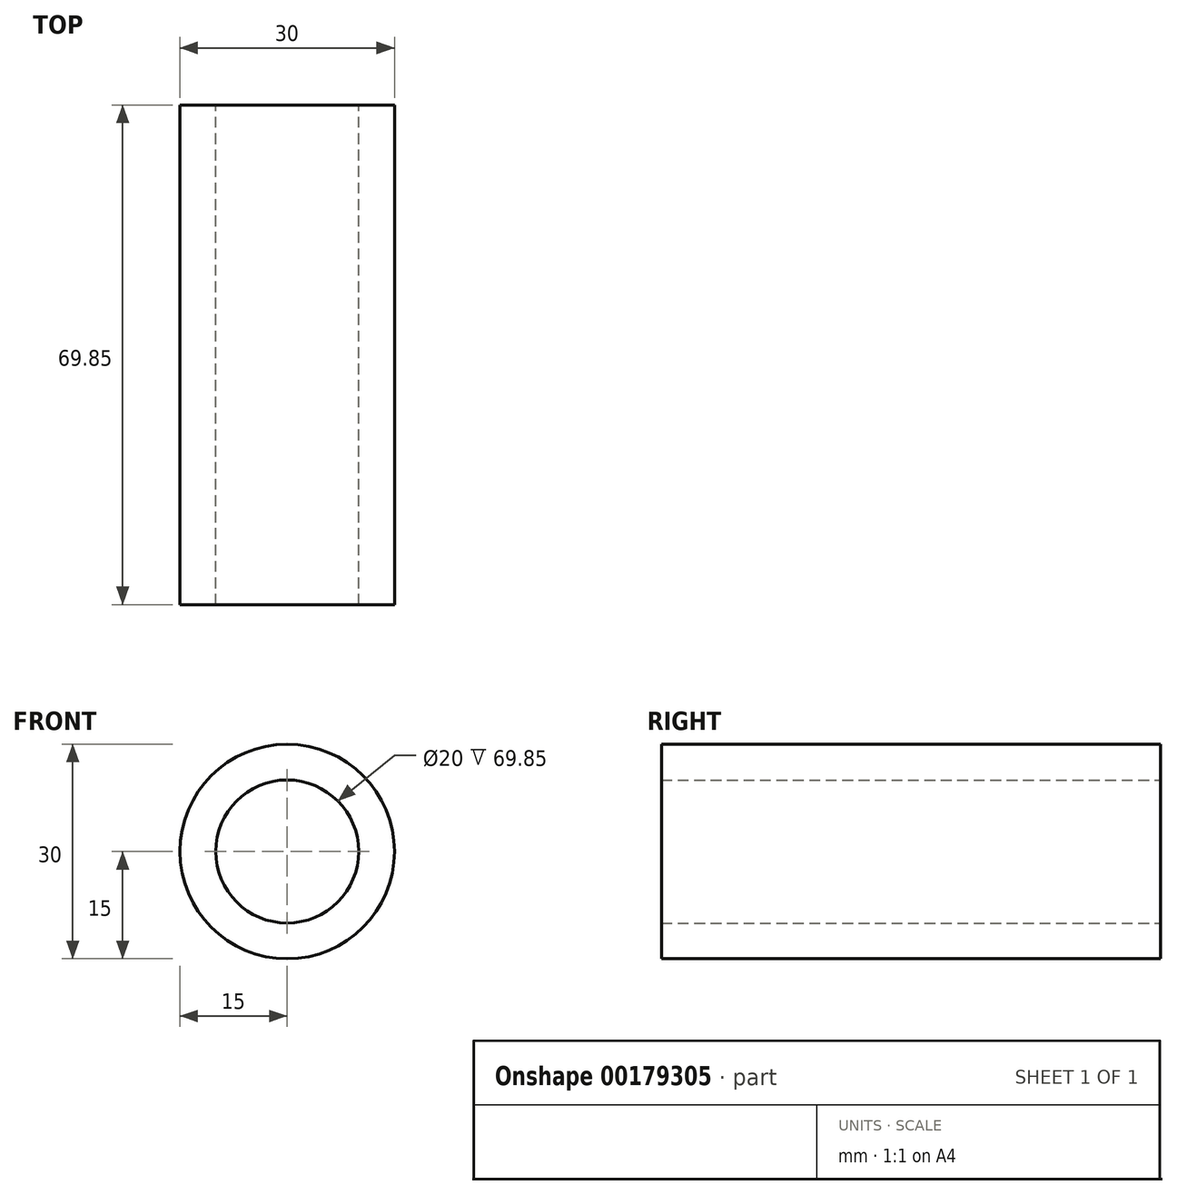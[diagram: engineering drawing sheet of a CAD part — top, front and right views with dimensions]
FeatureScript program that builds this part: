
annotation { "Feature Type Name" : "Feature", "Feature Type Description" : "" }
export const myFeature = defineFeature(function(context is Context, id is Id, definition is map)
    precondition{}
    {
        {
            var Q0;
            Q0=qCreatedBy(makeId("Front.planeOp"),FACE);
            var sketch = newSketch(context, id + "F0", { "sketchPlane" : qUnion([Q0])});
            skCircle(sketch, "E0", {"center": v(0, 0) * mm, "radius": 15 * mm});
            skCircle(sketch, "E1", {"center": v(0, 0) * mm, "radius": 10 * mm});
            skSolve(sketch);
        }
        {
            var Q0;
            Q0=makeQuery(id+"F0.imprint","IMPRINT",FACE,{"disambiguationData":[TD([[makeQuery(id+"F0.imprint","IMPRINT",EDGE,{"derivedFrom":sQuery(id+"F0.wireOp",EDGE,"E0")}),1.0]])]});
            extrude(context, id + "F1", {"entities" : qUnion([Q0]), "depth" : 69.85 * mm});
        }
    });
